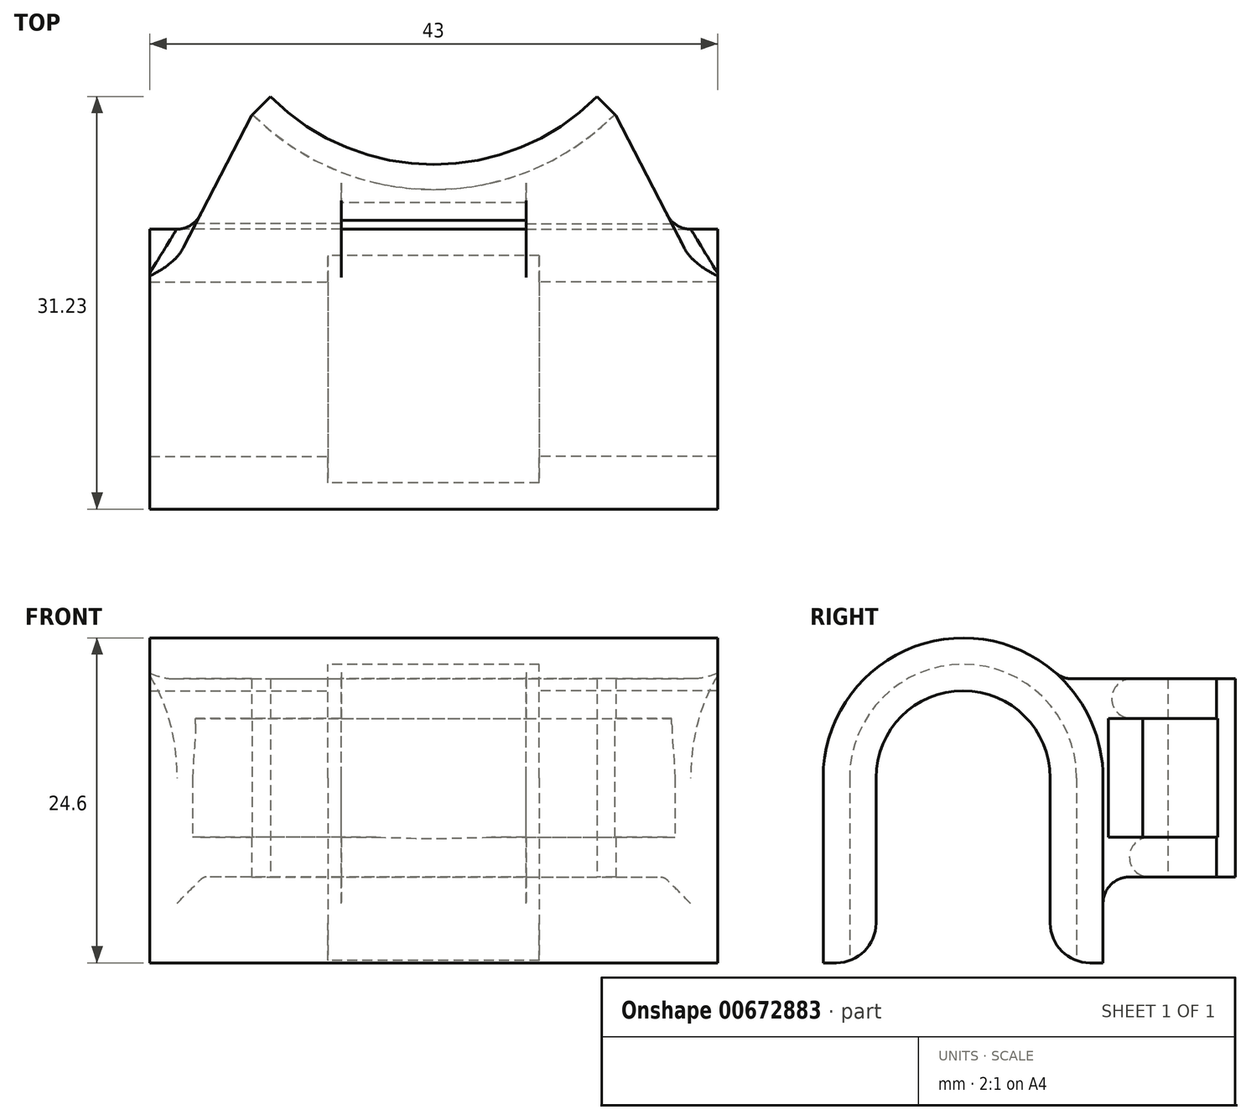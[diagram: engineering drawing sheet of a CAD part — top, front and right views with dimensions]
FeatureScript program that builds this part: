
annotation { "Feature Type Name" : "Feature", "Feature Type Description" : "" }
export const myFeature = defineFeature(function(context is Context, id is Id, definition is map)
    precondition{}
    {
        {
            var Q0;
            Q0=qCreatedBy(makeId("Top.planeOp"),FACE);
            var sketch = newSketch(context, id + "F0", { "sketchPlane" : qUnion([Q0])});
            skArc(sketch, "E0", {"start": v(12.37, -12.37) * mm, "mid": v(6.7, -16.17) * mm, "end": v(0, -17.5) * mm});
            skLineSegment(sketch, "E1", {"start": v(0, -17.5) * mm, "end": v(0, -25.8) * mm});
            skLineSegment(sketch, "E2", {"start": v(13.79, -13.79) * mm, "end": v(12.37, -12.37) * mm});
            skLineSegment(sketch, "E3", {"start": v(20, -25.8) * mm, "end": v(0, -25.8) * mm});
            skLineSegment(sketch, "E4", {"start": v(13.79, -13.79) * mm, "end": v(20, -25.8) * mm});
            skSolve(sketch);
        }
        {
            var Q0;
            Q0 = qSketchRegion(id + "F0", true);
            extrude(context, id + "F1", {"entities" : qUnion([Q0]), "endBound" : BoundingType.SYMMETRIC, "depth" : 15 * mm, "offsetDistance" : 25 * mm});
        }
        {
            var Q0;
            Q0=qCreatedBy(makeId("Top.planeOp"),FACE);
            var sketch = newSketch(context, id + "F2", { "sketchPlane" : qUnion([Q0])});
            skLineSegment(sketch, "E5.0", {"start": v(13.79, -13.79) * mm, "end": v(13.72, -13.72) * mm});
            skLineSegment(sketch, "E6", {"start": v(0, -19.4) * mm, "end": v(0, -22) * mm});
            skLineSegment(sketch, "E7", {"start": v(0, -22) * mm, "end": v(18.03, -22) * mm});
            skArc(sketch, "E8.0", {"start": v(13.72, -13.72) * mm, "mid": v(7.42, -17.92) * mm, "end": v(0, -19.4) * mm});
            skLineSegment(sketch, "E9", {"start": v(18.03, -22) * mm, "end": v(13.79, -13.79) * mm});
            skSolve(sketch);
        }
        {
            var Q0;
            Q0 = qSketchRegion(id + "F2", true);
            extrude(context, id + "F3", {"entities" : qUnion([Q0]), "operationType" : NewBodyOperationType.REMOVE, "endBound" : BoundingType.SYMMETRIC, "oppositeDirection" : true, "depth" : 9 * mm, "offsetDistance" : 25 * mm});
        }
        {
            var Q0;
            Q0=qCreatedBy(makeId("Right.planeOp"),FACE);
            var sketch = newSketch(context, id + "F4", { "sketchPlane" : qUnion([Q0])});
            skArc(sketch, "E10", {"start": v(-26.4, 0) * mm, "mid": v(-33, 6.6) * mm, "end": v(-39.6, 0) * mm});
            skArc(sketch, "E11", {"start": v(-22.4, 0) * mm, "mid": v(-33, 10.6) * mm, "end": v(-43.6, 0) * mm});
            skLineSegment(sketch, "E12", {"start": v(-26.4, 0) * mm, "end": v(-26.4, -14) * mm});
            skLineSegment(sketch, "E13", {"start": v(-26.4, -14) * mm, "end": v(-22.4, -14) * mm});
            skLineSegment(sketch, "E14", {"start": v(-22.4, -14) * mm, "end": v(-22.4, 0) * mm});
            skLineSegment(sketch, "E15", {"start": v(-39.6, 0) * mm, "end": v(-39.6, -14) * mm});
            skLineSegment(sketch, "E16", {"start": v(-39.6, -14) * mm, "end": v(-43.6, -14) * mm});
            skLineSegment(sketch, "E17", {"start": v(-43.6, -14) * mm, "end": v(-43.6, 0) * mm});
            skSolve(sketch);
        }
        {
            var Q0;
            Q0 = qSketchRegion(id + "F4", true);
            extrude(context, id + "F5", {"entities" : qUnion([Q0]), "operationType" : NewBodyOperationType.ADD, "depth" : 21.5 * mm, "offsetDistance" : 25 * mm});
        }
        {
            var Q0;
            Q0=qCreatedBy(makeId("Right.planeOp"),FACE);
            var sketch = newSketch(context, id + "F6", { "sketchPlane" : qUnion([Q0])});
            skArc(sketch, "E18.0", {"start": v(-22.4, 0) * mm, "mid": v(-33, 10.6) * mm, "end": v(-43.6, 0) * mm});
            skArc(sketch, "E19.0", {"start": v(-20.4, 0) * mm, "mid": v(-29.45, 12.09) * mm, "end": v(-43.6, 6.81) * mm});
            skLineSegment(sketch, "E20", {"start": v(-22.4, -14) * mm, "end": v(-22.4, 0) * mm});
            skLineSegment(sketch, "E21", {"start": v(-43.6, 0) * mm, "end": v(-43.6, 6.81) * mm});
            skLineSegment(sketch, "E22", {"start": v(-20.4, 0) * mm, "end": v(-20.4, -14) * mm});
            skLineSegment(sketch, "E23", {"start": v(-20.4, -14) * mm, "end": v(-22.4, -14) * mm});
            skSolve(sketch);
        }
        {
            var Q0;
            Q0 = qSketchRegion(id + "F6", true);
            extrude(context, id + "F7", {"entities" : qUnion([Q0]), "operationType" : NewBodyOperationType.REMOVE, "depth" : 7 * mm, "offsetDistance" : 25 * mm});
        }
        {
            var Q0;
            Q0=qCreatedBy(makeId("Right.planeOp"),FACE);
            var sketch = newSketch(context, id + "F8", { "sketchPlane" : qUnion([Q0])});
            skLineSegment(sketch, "E24.0", {"start": v(-26.4, 0) * mm, "end": v(-26.4, -14) * mm});
            skArc(sketch, "E25.0", {"start": v(-26.4, 0) * mm, "mid": v(-33, 6.6) * mm, "end": v(-39.6, 0) * mm});
            skLineSegment(sketch, "E26.0", {"start": v(-39.6, 0) * mm, "end": v(-39.6, -14) * mm});
            skLineSegment(sketch, "E27.0", {"start": v(-24.4, 0) * mm, "end": v(-24.4, -14) * mm});
            skArc(sketch, "E27.1", {"start": v(-24.4, 0) * mm, "mid": v(-33, 8.6) * mm, "end": v(-41.6, 0) * mm});
            skLineSegment(sketch, "E27.2", {"start": v(-41.6, 0) * mm, "end": v(-41.6, -14) * mm});
            skLineSegment(sketch, "E28", {"start": v(-24.4, -14) * mm, "end": v(-26.4, -14) * mm});
            skLineSegment(sketch, "E29", {"start": v(-39.6, -14) * mm, "end": v(-41.6, -14) * mm});
            skSolve(sketch);
        }
        {
            var Q0;
            Q0 = qSketchRegion(id + "F8", true);
            extrude(context, id + "F9", {"entities" : qUnion([Q0]), "operationType" : NewBodyOperationType.REMOVE, "depth" : 8 * mm, "offsetDistance" : 25 * mm});
        }
        {
            var Q0;
            Q0=makeQuery(id+"F5.opExtrude","SWEPT_EDGE",EDGE,{"disambiguationData":[OSD([sQuery(id+"F4.wireOp",EDGE,"E12"),sQuery(id+"F4.wireOp",EDGE,"E13")])]});
            var Q1;
            Q1=makeQuery(id+"F5.opExtrude","SWEPT_EDGE",EDGE,{"disambiguationData":[OSD([sQuery(id+"F4.wireOp",EDGE,"E15"),sQuery(id+"F4.wireOp",EDGE,"E16")])]});
            fillet(context, id + "F10", {"entities" : qUnion([Q0, Q1]), "radius" : 3 * mm, "tangentPropagation" : true, "allowEdgeOverflow" : false});
        }
        {
            var Q0;
            Q0=makeQuery(id+"F3.boolean.opBoolean","COPY",EDGE,{"derivedFrom":makeQuery(id+"F3.opExtrude","SWEPT_EDGE",EDGE,{"disambiguationData":[OSD([sQuery(id+"F2.wireOp",EDGE,"E5.0"),sQuery(id+"F2.wireOp",EDGE,"E8.0")])]})});
            var Q1;
            Q1=makeQuery(id+"F7.boolean.opBoolean","INTERSECT",EDGE,{"derivedFrom":[makeQuery(id+"F3.boolean.opBoolean","COPY",FACE,{"derivedFrom":makeQuery(id+"F3.opExtrude","CAP_FACE",FACE,{"disambiguationData":[OSD([sQuery(id+"F2.wireOp",EDGE,"E5.0"),sQuery(id+"F2.wireOp",EDGE,"E6"),sQuery(id+"F2.wireOp",EDGE,"E7"),sQuery(id+"F2.wireOp",EDGE,"E8.0"),sQuery(id+"F2.wireOp",EDGE,"E9")])],"isStart":true})}),makeQuery(id+"F7.opExtrude","SWEPT_FACE",FACE,{"disambiguationData":[OSD([sQuery(id+"F6.wireOp",EDGE,"E19.0")])]})]});
            var Q2;
            Q2=makeQuery(id+"F7.boolean.opBoolean","INTERSECT",EDGE,{"derivedFrom":[makeQuery(id+"F1.opExtrude","CAP_FACE",FACE,{"disambiguationData":[OSD([sQuery(id+"F0.wireOp",EDGE,"E0"),sQuery(id+"F0.wireOp",EDGE,"E1"),sQuery(id+"F0.wireOp",EDGE,"E2"),sQuery(id+"F0.wireOp",EDGE,"E3"),sQuery(id+"F0.wireOp",EDGE,"E4")])],"isStart":true}),makeQuery(id+"F7.opExtrude","SWEPT_FACE",FACE,{"disambiguationData":[OSD([sQuery(id+"F6.wireOp",EDGE,"E22")])]})]});
            var Q3;
            Q3=makeQuery(id+"F7.boolean.opBoolean","INTERSECT",EDGE,{"derivedFrom":[makeQuery(id+"F1.opExtrude","CAP_FACE",FACE,{"disambiguationData":[OSD([sQuery(id+"F0.wireOp",EDGE,"E0"),sQuery(id+"F0.wireOp",EDGE,"E1"),sQuery(id+"F0.wireOp",EDGE,"E2"),sQuery(id+"F0.wireOp",EDGE,"E3"),sQuery(id+"F0.wireOp",EDGE,"E4")])],"isStart":false}),makeQuery(id+"F7.opExtrude","SWEPT_FACE",FACE,{"disambiguationData":[OSD([sQuery(id+"F6.wireOp",EDGE,"E19.0")])]})]});
            var Q4;
            Q4=makeQuery(id+"F7.boolean.opBoolean","INTERSECT",EDGE,{"derivedFrom":[makeQuery(id+"F3.boolean.opBoolean","COPY",FACE,{"derivedFrom":makeQuery(id+"F3.opExtrude","CAP_FACE",FACE,{"disambiguationData":[OSD([sQuery(id+"F2.wireOp",EDGE,"E5.0"),sQuery(id+"F2.wireOp",EDGE,"E6"),sQuery(id+"F2.wireOp",EDGE,"E7"),sQuery(id+"F2.wireOp",EDGE,"E8.0"),sQuery(id+"F2.wireOp",EDGE,"E9")])],"isStart":false})}),makeQuery(id+"F7.opExtrude","SWEPT_FACE",FACE,{"disambiguationData":[OSD([sQuery(id+"F6.wireOp",EDGE,"E22")])]})]});
            fillet(context, id + "F11", {"entities" : qUnion([Q0, Q1, Q2, Q3, Q4]), "radius" : 1.5 * mm, "tangentPropagation" : true, "allowEdgeOverflow" : false});
        }
        {
            var Q0;
            Q0=makeQuery(id+"F5.boolean.opBoolean","INTERSECT",EDGE,{"derivedFrom":[makeQuery(id+"F1.opExtrude","CAP_FACE",FACE,{"disambiguationData":[OSD([sQuery(id+"F0.wireOp",EDGE,"E0"),sQuery(id+"F0.wireOp",EDGE,"E1"),sQuery(id+"F0.wireOp",EDGE,"E2"),sQuery(id+"F0.wireOp",EDGE,"E3"),sQuery(id+"F0.wireOp",EDGE,"E4")])],"isStart":true}),makeQuery(id+"F5.opExtrude","SWEPT_FACE",FACE,{"disambiguationData":[OSD([sQuery(id+"F4.wireOp",EDGE,"E14")])]})]});
            var Q1;
            Q1=makeQuery(id+"F5.boolean.opBoolean","INTERSECT",EDGE,{"derivedFrom":[makeQuery(id+"F1.opExtrude","SWEPT_FACE",FACE,{"disambiguationData":[OSD([sQuery(id+"F0.wireOp",EDGE,"E4")])]}),makeQuery(id+"F5.opExtrude","SWEPT_FACE",FACE,{"disambiguationData":[OSD([sQuery(id+"F4.wireOp",EDGE,"E14")])]})]});
            var Q2;
            Q2=makeQuery(id+"F5.boolean.opBoolean","INTERSECT",EDGE,{"derivedFrom":[makeQuery(id+"F1.opExtrude","CAP_FACE",FACE,{"disambiguationData":[OSD([sQuery(id+"F0.wireOp",EDGE,"E0"),sQuery(id+"F0.wireOp",EDGE,"E1"),sQuery(id+"F0.wireOp",EDGE,"E2"),sQuery(id+"F0.wireOp",EDGE,"E3"),sQuery(id+"F0.wireOp",EDGE,"E4")])],"isStart":false}),makeQuery(id+"F5.opExtrude","SWEPT_FACE",FACE,{"disambiguationData":[OSD([sQuery(id+"F4.wireOp",EDGE,"E11")])]})]});
            fillet(context, id + "F12", {"entities" : qUnion([Q0, Q1, Q2]), "radius" : 2 * mm, "tangentPropagation" : true, "allowEdgeOverflow" : false});
        }
        {
            var Q0;
            Q0=makeQuery(id+"F1.opExtrude","SWEPT_BODY",BODY,{"disambiguationData":[OSD([sQuery(id+"F0.wireOp",EDGE,"E0"),sQuery(id+"F0.wireOp",EDGE,"E1"),sQuery(id+"F0.wireOp",EDGE,"E2"),sQuery(id+"F0.wireOp",EDGE,"olI25vU3-2vOF-bSCl-7s6G-gbXyEdqE54Xj"),sQuery(id+"F0.wireOp",EDGE,"LtZ7SRg4-OnZj-E5Z2-ffiz-tNcVvZ1VUXdi"),sQuery(id+"F0.wireOp",EDGE,"E3")])]});
            var Q1;
            Q1=qCreatedBy(makeId("Right.planeOp"),FACE);
            mirror(context, id + "F13", {"operationType" : NewBodyOperationType.ADD, "entities" : qUnion([Q0]), "mirrorPlane" : qUnion([Q1])});
        }
    });
